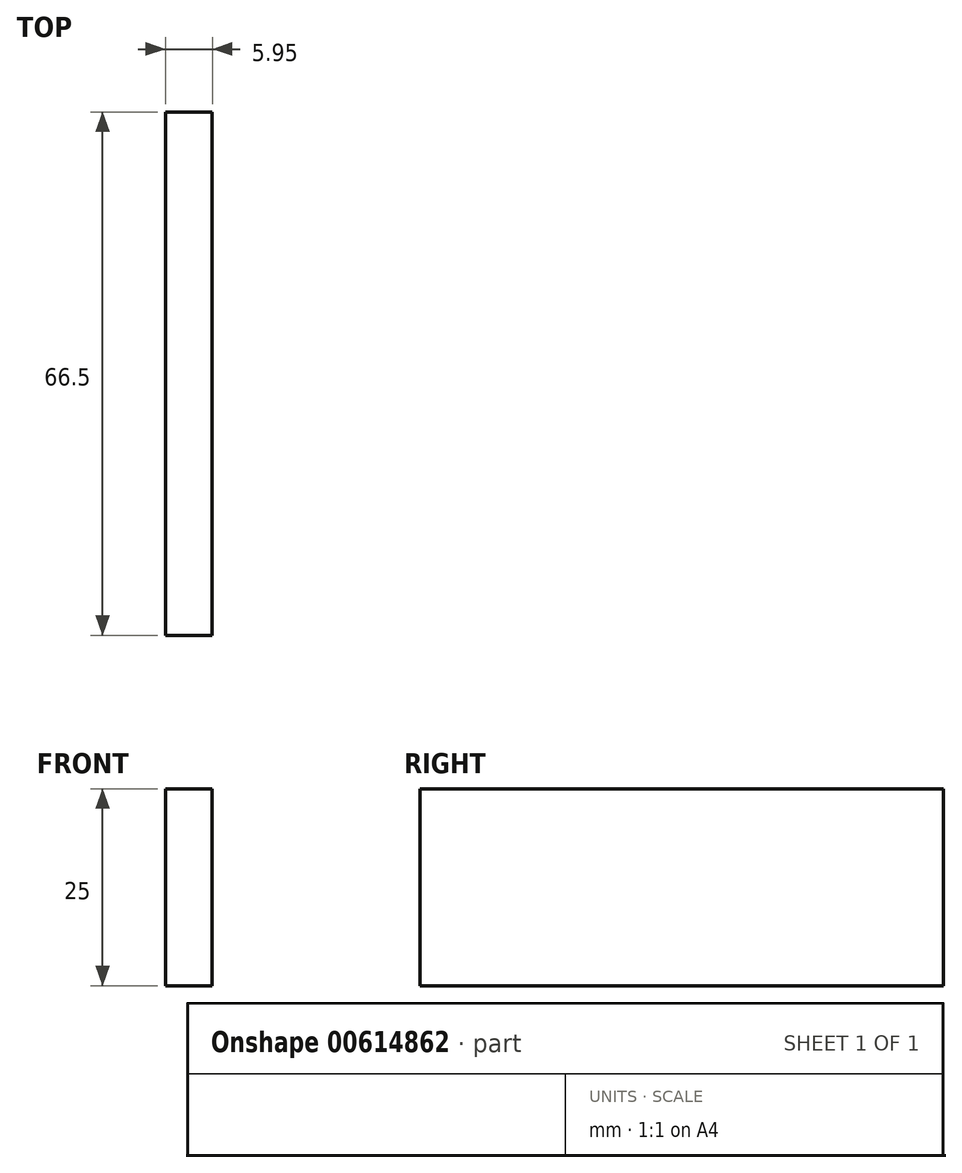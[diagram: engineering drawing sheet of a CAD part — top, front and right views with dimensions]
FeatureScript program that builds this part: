
annotation { "Feature Type Name" : "Feature", "Feature Type Description" : "" }
export const myFeature = defineFeature(function(context is Context, id is Id, definition is map)
    precondition{}
    {
        {
            var Q0;
            Q0=qCreatedBy(makeId("Top.planeOp"),FACE);
            var sketch = newSketch(context, id + "F0", { "sketchPlane" : qUnion([Q0])});
            skLineSegment(sketch, "E0.bottom", {"start": v(-68.35, 46.7) * mm, "end": v(59.06, 46.7) * mm});
            skLineSegment(sketch, "E0.top", {"start": v(-68.35, -19.8) * mm, "end": v(59.06, -19.8) * mm});
            skLineSegment(sketch, "E0.left", {"start": v(-68.35, 46.7) * mm, "end": v(-68.35, -19.8) * mm});
            skLineSegment(sketch, "E0.right", {"start": v(59.06, 46.7) * mm, "end": v(59.06, -19.8) * mm});
            skSolve(sketch);
        }
        {
            var Q0;
            Q0=sQuery(id+"F0.wireOp",EDGE,"E0.right");
            var Q1;
            Q1=sQuery(id+"F0.wireOp",EDGE,"E0.left");
            var Q2;
            Q2=sQuery(id+"F0.wireOp",EDGE,"E0.top");
            var Q3;
            Q3=sQuery(id+"F0.wireOp",EDGE,"E0.bottom");
            extrude(context, id + "F1", {"bodyType" : ToolBodyType.SURFACE, "surfaceEntities" : qUnion([Q0, Q1, Q2, Q3]), "depth" : 25 * mm, "offsetDistance" : 25.4 * mm});
        }
        {
            var Q0;
            Q0 = qSketchRegion(id + "FgJJTjobEy7aKqz_1", true);
            var Q1;
            Q1=makeQuery(id+"F1.opExtrude","SWEPT_FACE",FACE,{"disambiguationData":[OSD([sQuery(id+"F0.wireOp",EDGE,"E0.right")])]});
            extrude(context, id + "F2", {"entities" : qUnion([Q0, Q1]), "oppositeDirection" : true, "depth" : 5.95 * mm, "offsetDistance" : 25.4 * mm});
        }
    });
